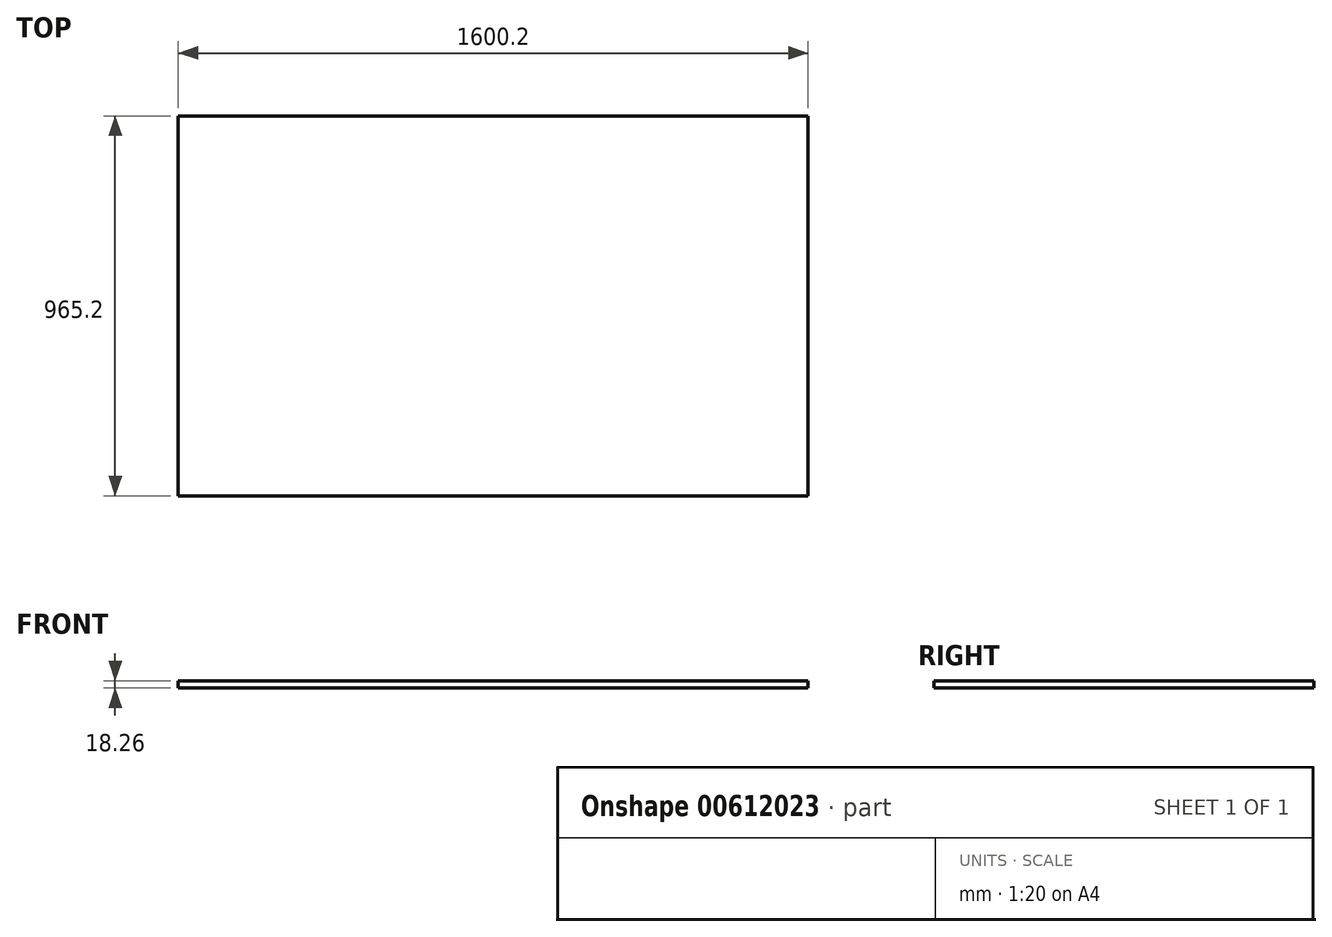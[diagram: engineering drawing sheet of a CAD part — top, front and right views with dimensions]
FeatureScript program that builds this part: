
annotation { "Feature Type Name" : "Feature", "Feature Type Description" : "" }
export const myFeature = defineFeature(function(context is Context, id is Id, definition is map)
    precondition{}
    {
        {
            var Q0;
            Q0=qCreatedBy(makeId("Top.planeOp"),FACE);
            var sketch = newSketch(context, id + "F0", { "sketchPlane" : qUnion([Q0])});
            skLineSegment(sketch, "E0.bottom", {"start": v(-1503.36, 956.1) * mm, "end": v(96.84, 956.1) * mm});
            skLineSegment(sketch, "E0.top", {"start": v(-1503.36, -9.1) * mm, "end": v(96.84, -9.1) * mm});
            skLineSegment(sketch, "E0.left", {"start": v(-1503.36, 956.1) * mm, "end": v(-1503.36, -9.1) * mm});
            skLineSegment(sketch, "E0.right", {"start": v(96.84, 956.1) * mm, "end": v(96.84, -9.1) * mm});
            skLineSegment(sketch, "E1", {"start": v(-1503.36, -9.1) * mm, "end": v(-1363.66, -9.1) * mm, "construction": true});
            skLineSegment(sketch, "E2", {"start": v(-1363.66, -9.1) * mm, "end": v(-1363.66, 956.1) * mm, "construction": true});
            skLineSegment(sketch, "E3", {"start": v(96.84, 956.1) * mm, "end": v(-42.86, 956.1) * mm, "construction": true});
            skLineSegment(sketch, "E4", {"start": v(-42.86, 956.1) * mm, "end": v(-42.86, -9.1) * mm, "construction": true});
            skLineSegment(sketch, "E5", {"start": v(96.84, -9.1) * mm, "end": v(96.84, 130.6) * mm, "construction": true});
            skLineSegment(sketch, "E6", {"start": v(96.84, 130.6) * mm, "end": v(-1503.36, 130.6) * mm, "construction": true});
            skLineSegment(sketch, "E7", {"start": v(-1503.36, 956.1) * mm, "end": v(-1503.36, 816.4) * mm, "construction": true});
            skLineSegment(sketch, "E8", {"start": v(-1503.36, 816.4) * mm, "end": v(96.84, 816.4) * mm, "construction": true});
            skPoint(sketch, "E9", {"position": v(-1363.66, 816.4) * mm});
            skPoint(sketch, "E10", {"position": v(-1363.66, 130.6) * mm});
            skPoint(sketch, "E11", {"position": v(-42.86, 130.6) * mm});
            skPoint(sketch, "E12", {"position": v(-42.86, 816.4) * mm});
            skLineSegment(sketch, "E13", {"start": v(-1363.66, 816.4) * mm, "end": v(-1363.66, 803.7) * mm, "construction": true});
            skLineSegment(sketch, "E14", {"start": v(-1363.66, 803.7) * mm, "end": v(-1350.96, 803.7) * mm, "construction": true});
            skLineSegment(sketch, "E15", {"start": v(-1350.96, 803.7) * mm, "end": v(-1350.96, 816.4) * mm, "construction": true});
            skLineSegment(sketch, "E16", {"start": v(-42.86, 816.4) * mm, "end": v(-55.56, 816.4) * mm, "construction": true});
            skLineSegment(sketch, "E17", {"start": v(-55.56, 816.4) * mm, "end": v(-55.56, 803.7) * mm, "construction": true});
            skLineSegment(sketch, "E18", {"start": v(-1363.66, 130.6) * mm, "end": v(-1350.96, 130.6) * mm});
            skLineSegment(sketch, "E19", {"start": v(-1350.96, 130.6) * mm, "end": v(-1350.96, 143.3) * mm});
            skLineSegment(sketch, "E20", {"start": v(-42.86, 130.6) * mm, "end": v(-55.56, 130.6) * mm});
            skLineSegment(sketch, "E21", {"start": v(-55.56, 130.6) * mm, "end": v(-55.56, 143.3) * mm});
            skLineSegment(sketch, "E22", {"start": v(-1350.96, 143.3) * mm, "end": v(-1122.36, 143.3) * mm});
            skLineSegment(sketch, "E23.0.1.0", {"start": v(-1350.96, 194.1) * mm, "end": v(-1122.36, 194.1) * mm});
            skLineSegment(sketch, "E23.0.2.0", {"start": v(-1350.96, 245.15) * mm, "end": v(-1122.36, 245.15) * mm});
            skLineSegment(sketch, "E23.0.3.0", {"start": v(-1350.96, 295.95) * mm, "end": v(-1122.36, 295.95) * mm});
            skLineSegment(sketch, "E23.0.4.0", {"start": v(-1350.96, 346.75) * mm, "end": v(-1122.36, 346.75) * mm});
            skLineSegment(sketch, "E23.0.5.0", {"start": v(-1350.96, 397.55) * mm, "end": v(-1122.36, 397.55) * mm});
            skLineSegment(sketch, "E23.0.6.0", {"start": v(-1350.96, 448.35) * mm, "end": v(-1122.36, 448.35) * mm});
            skLineSegment(sketch, "E23.0.7.0", {"start": v(-1350.96, 499.15) * mm, "end": v(-1122.36, 499.15) * mm});
            skLineSegment(sketch, "E23.1.0.0", {"start": v(-1300.16, 143.55) * mm, "end": v(-1071.56, 143.55) * mm});
            skLineSegment(sketch, "E23.1.1.0", {"start": v(-1300.16, 194.35) * mm, "end": v(-1071.56, 194.35) * mm});
            skLineSegment(sketch, "E23.1.2.0", {"start": v(-1300.16, 245.15) * mm, "end": v(-1071.56, 245.15) * mm});
            skLineSegment(sketch, "E23.1.3.0", {"start": v(-1300.16, 295.95) * mm, "end": v(-1071.56, 295.95) * mm});
            skLineSegment(sketch, "E23.1.4.0", {"start": v(-1300.16, 346.75) * mm, "end": v(-1071.56, 346.75) * mm});
            skLineSegment(sketch, "E23.1.5.0", {"start": v(-1300.16, 397.55) * mm, "end": v(-1071.56, 397.55) * mm});
            skLineSegment(sketch, "E23.1.6.0", {"start": v(-1300.16, 448.35) * mm, "end": v(-1071.56, 448.35) * mm});
            skLineSegment(sketch, "E23.1.7.0", {"start": v(-1300.16, 499.15) * mm, "end": v(-1071.56, 499.15) * mm});
            skLineSegment(sketch, "E23.2.0.0", {"start": v(-1249.36, 143.55) * mm, "end": v(-1020.76, 143.55) * mm});
            skLineSegment(sketch, "E23.2.1.0", {"start": v(-1249.36, 194.35) * mm, "end": v(-1020.76, 194.35) * mm});
            skLineSegment(sketch, "E23.2.2.0", {"start": v(-1249.36, 245.15) * mm, "end": v(-1020.76, 245.15) * mm});
            skLineSegment(sketch, "E23.2.3.0", {"start": v(-1249.36, 295.95) * mm, "end": v(-1020.76, 295.95) * mm});
            skLineSegment(sketch, "E23.2.4.0", {"start": v(-1249.36, 346.75) * mm, "end": v(-1020.76, 346.75) * mm});
            skLineSegment(sketch, "E23.2.5.0", {"start": v(-1249.36, 397.55) * mm, "end": v(-1020.76, 397.55) * mm});
            skLineSegment(sketch, "E23.2.6.0", {"start": v(-1249.36, 448.35) * mm, "end": v(-1020.76, 448.35) * mm});
            skLineSegment(sketch, "E23.2.7.0", {"start": v(-1249.36, 499.15) * mm, "end": v(-1020.76, 499.15) * mm});
            skLineSegment(sketch, "E23.3.0.0", {"start": v(-1198.56, 143.55) * mm, "end": v(-969.96, 143.55) * mm});
            skLineSegment(sketch, "E23.3.1.0", {"start": v(-1198.56, 194.35) * mm, "end": v(-969.96, 194.35) * mm});
            skLineSegment(sketch, "E23.3.2.0", {"start": v(-1198.56, 245.15) * mm, "end": v(-969.96, 245.15) * mm});
            skLineSegment(sketch, "E23.3.3.0", {"start": v(-1198.56, 295.95) * mm, "end": v(-969.96, 295.95) * mm});
            skLineSegment(sketch, "E23.3.4.0", {"start": v(-1198.56, 346.75) * mm, "end": v(-969.96, 346.75) * mm});
            skLineSegment(sketch, "E23.3.5.0", {"start": v(-1198.56, 397.55) * mm, "end": v(-969.96, 397.55) * mm});
            skLineSegment(sketch, "E23.3.6.0", {"start": v(-1198.56, 448.35) * mm, "end": v(-969.96, 448.35) * mm});
            skLineSegment(sketch, "E23.3.7.0", {"start": v(-1198.56, 499.15) * mm, "end": v(-969.96, 499.15) * mm});
            skLineSegment(sketch, "E23.4.0.0", {"start": v(-1147.76, 143.55) * mm, "end": v(-919.16, 143.55) * mm});
            skLineSegment(sketch, "E23.4.1.0", {"start": v(-1147.76, 194.35) * mm, "end": v(-919.16, 194.35) * mm});
            skLineSegment(sketch, "E23.4.2.0", {"start": v(-1147.76, 245.15) * mm, "end": v(-919.16, 245.15) * mm});
            skLineSegment(sketch, "E23.4.3.0", {"start": v(-1147.76, 295.95) * mm, "end": v(-919.16, 295.95) * mm});
            skLineSegment(sketch, "E23.4.4.0", {"start": v(-1147.76, 346.75) * mm, "end": v(-919.16, 346.75) * mm});
            skLineSegment(sketch, "E23.4.5.0", {"start": v(-1147.76, 397.55) * mm, "end": v(-919.16, 397.55) * mm});
            skLineSegment(sketch, "E23.4.6.0", {"start": v(-1147.76, 448.35) * mm, "end": v(-919.16, 448.35) * mm});
            skLineSegment(sketch, "E23.4.7.0", {"start": v(-1147.76, 499.15) * mm, "end": v(-919.16, 499.15) * mm});
            skLineSegment(sketch, "E23.5.0.0", {"start": v(-1096.96, 143.55) * mm, "end": v(-868.36, 143.55) * mm});
            skLineSegment(sketch, "E23.5.1.0", {"start": v(-1096.96, 194.35) * mm, "end": v(-868.36, 194.35) * mm});
            skLineSegment(sketch, "E23.5.2.0", {"start": v(-1096.96, 245.15) * mm, "end": v(-868.36, 245.15) * mm});
            skLineSegment(sketch, "E23.5.3.0", {"start": v(-1096.96, 295.95) * mm, "end": v(-868.36, 295.95) * mm});
            skLineSegment(sketch, "E23.5.4.0", {"start": v(-1096.96, 346.75) * mm, "end": v(-868.36, 346.75) * mm});
            skLineSegment(sketch, "E23.5.5.0", {"start": v(-1096.96, 397.55) * mm, "end": v(-868.36, 397.55) * mm});
            skLineSegment(sketch, "E23.5.6.0", {"start": v(-1096.96, 448.35) * mm, "end": v(-868.36, 448.35) * mm});
            skLineSegment(sketch, "E23.5.7.0", {"start": v(-1096.96, 499.15) * mm, "end": v(-868.36, 499.15) * mm});
            skLineSegment(sketch, "E23.6.0.0", {"start": v(-1046.16, 143.55) * mm, "end": v(-817.56, 143.55) * mm});
            skLineSegment(sketch, "E23.6.1.0", {"start": v(-1046.16, 194.35) * mm, "end": v(-817.56, 194.35) * mm});
            skLineSegment(sketch, "E23.6.2.0", {"start": v(-1046.16, 245.15) * mm, "end": v(-817.56, 245.15) * mm});
            skLineSegment(sketch, "E23.6.3.0", {"start": v(-1046.16, 295.95) * mm, "end": v(-817.56, 295.95) * mm});
            skLineSegment(sketch, "E23.6.4.0", {"start": v(-1046.16, 346.75) * mm, "end": v(-817.56, 346.75) * mm});
            skLineSegment(sketch, "E23.6.5.0", {"start": v(-1046.16, 397.55) * mm, "end": v(-817.56, 397.55) * mm});
            skLineSegment(sketch, "E23.6.6.0", {"start": v(-1046.16, 448.35) * mm, "end": v(-817.56, 448.35) * mm});
            skLineSegment(sketch, "E23.6.7.0", {"start": v(-1046.16, 499.15) * mm, "end": v(-817.56, 499.15) * mm});
            skLineSegment(sketch, "E23.7.0.0", {"start": v(-995.36, 143.55) * mm, "end": v(-766.76, 143.55) * mm});
            skLineSegment(sketch, "E23.7.1.0", {"start": v(-995.36, 194.35) * mm, "end": v(-766.76, 194.35) * mm});
            skLineSegment(sketch, "E23.7.2.0", {"start": v(-995.36, 245.15) * mm, "end": v(-766.76, 245.15) * mm});
            skLineSegment(sketch, "E23.7.3.0", {"start": v(-995.36, 295.95) * mm, "end": v(-766.76, 295.95) * mm});
            skLineSegment(sketch, "E23.7.4.0", {"start": v(-995.36, 346.75) * mm, "end": v(-766.76, 346.75) * mm});
            skLineSegment(sketch, "E23.7.5.0", {"start": v(-995.36, 397.55) * mm, "end": v(-766.76, 397.55) * mm});
            skLineSegment(sketch, "E23.7.6.0", {"start": v(-995.36, 448.35) * mm, "end": v(-766.76, 448.35) * mm});
            skLineSegment(sketch, "E23.7.7.0", {"start": v(-995.36, 499.15) * mm, "end": v(-766.76, 499.15) * mm});
            skLineSegment(sketch, "E23.8.0.0", {"start": v(-944.56, 143.55) * mm, "end": v(-715.96, 143.55) * mm});
            skLineSegment(sketch, "E23.8.1.0", {"start": v(-944.56, 194.35) * mm, "end": v(-715.96, 194.35) * mm});
            skLineSegment(sketch, "E23.8.2.0", {"start": v(-944.56, 245.15) * mm, "end": v(-715.96, 245.15) * mm});
            skLineSegment(sketch, "E23.8.3.0", {"start": v(-944.56, 295.95) * mm, "end": v(-715.96, 295.95) * mm});
            skLineSegment(sketch, "E23.8.4.0", {"start": v(-944.56, 346.75) * mm, "end": v(-715.96, 346.75) * mm});
            skLineSegment(sketch, "E23.8.5.0", {"start": v(-944.56, 397.55) * mm, "end": v(-715.96, 397.55) * mm});
            skLineSegment(sketch, "E23.8.6.0", {"start": v(-944.56, 448.35) * mm, "end": v(-715.96, 448.35) * mm});
            skLineSegment(sketch, "E23.8.7.0", {"start": v(-944.56, 499.15) * mm, "end": v(-715.96, 499.15) * mm});
            skLineSegment(sketch, "E23.9.0.0", {"start": v(-893.76, 143.55) * mm, "end": v(-665.16, 143.55) * mm});
            skLineSegment(sketch, "E23.9.1.0", {"start": v(-893.76, 194.35) * mm, "end": v(-665.16, 194.35) * mm});
            skLineSegment(sketch, "E23.9.2.0", {"start": v(-893.76, 245.15) * mm, "end": v(-665.16, 245.15) * mm});
            skLineSegment(sketch, "E23.9.3.0", {"start": v(-893.76, 295.95) * mm, "end": v(-665.16, 295.95) * mm});
            skLineSegment(sketch, "E23.9.4.0", {"start": v(-893.76, 346.75) * mm, "end": v(-665.16, 346.75) * mm});
            skLineSegment(sketch, "E23.9.5.0", {"start": v(-893.76, 397.55) * mm, "end": v(-665.16, 397.55) * mm});
            skLineSegment(sketch, "E23.9.6.0", {"start": v(-893.76, 448.35) * mm, "end": v(-665.16, 448.35) * mm});
            skLineSegment(sketch, "E23.9.7.0", {"start": v(-893.76, 499.15) * mm, "end": v(-665.16, 499.15) * mm});
            skLineSegment(sketch, "E23.10.0.0", {"start": v(-842.96, 143.55) * mm, "end": v(-614.36, 143.55) * mm});
            skLineSegment(sketch, "E23.10.1.0", {"start": v(-842.96, 194.35) * mm, "end": v(-614.36, 194.35) * mm});
            skLineSegment(sketch, "E23.10.2.0", {"start": v(-842.96, 245.15) * mm, "end": v(-614.36, 245.15) * mm});
            skLineSegment(sketch, "E23.10.3.0", {"start": v(-842.96, 295.95) * mm, "end": v(-614.36, 295.95) * mm});
            skLineSegment(sketch, "E23.10.4.0", {"start": v(-842.96, 346.75) * mm, "end": v(-614.36, 346.75) * mm});
            skLineSegment(sketch, "E23.10.5.0", {"start": v(-842.96, 397.55) * mm, "end": v(-614.36, 397.55) * mm});
            skLineSegment(sketch, "E23.10.6.0", {"start": v(-842.96, 448.35) * mm, "end": v(-614.36, 448.35) * mm});
            skLineSegment(sketch, "E23.10.7.0", {"start": v(-842.96, 499.15) * mm, "end": v(-614.36, 499.15) * mm});
            skLineSegment(sketch, "E23.11.0.0", {"start": v(-792.16, 143.55) * mm, "end": v(-563.56, 143.55) * mm});
            skLineSegment(sketch, "E23.11.1.0", {"start": v(-792.16, 194.35) * mm, "end": v(-563.56, 194.35) * mm});
            skLineSegment(sketch, "E23.11.2.0", {"start": v(-792.16, 245.15) * mm, "end": v(-563.56, 245.15) * mm});
            skLineSegment(sketch, "E23.11.3.0", {"start": v(-792.16, 295.95) * mm, "end": v(-563.56, 295.95) * mm});
            skLineSegment(sketch, "E23.11.4.0", {"start": v(-792.16, 346.75) * mm, "end": v(-563.56, 346.75) * mm});
            skLineSegment(sketch, "E23.11.5.0", {"start": v(-792.16, 397.55) * mm, "end": v(-563.56, 397.55) * mm});
            skLineSegment(sketch, "E23.11.6.0", {"start": v(-792.16, 448.35) * mm, "end": v(-563.56, 448.35) * mm});
            skLineSegment(sketch, "E23.11.7.0", {"start": v(-792.16, 499.15) * mm, "end": v(-563.56, 499.15) * mm});
            skLineSegment(sketch, "E23.12.0.0", {"start": v(-741.36, 143.55) * mm, "end": v(-512.76, 143.55) * mm});
            skLineSegment(sketch, "E23.12.1.0", {"start": v(-741.36, 194.35) * mm, "end": v(-512.76, 194.35) * mm});
            skLineSegment(sketch, "E23.12.2.0", {"start": v(-741.36, 245.15) * mm, "end": v(-512.76, 245.15) * mm});
            skLineSegment(sketch, "E23.12.3.0", {"start": v(-741.36, 295.95) * mm, "end": v(-512.76, 295.95) * mm});
            skLineSegment(sketch, "E23.12.4.0", {"start": v(-741.36, 346.75) * mm, "end": v(-512.76, 346.75) * mm});
            skLineSegment(sketch, "E23.12.5.0", {"start": v(-741.36, 397.55) * mm, "end": v(-512.76, 397.55) * mm});
            skLineSegment(sketch, "E23.12.6.0", {"start": v(-741.36, 448.35) * mm, "end": v(-512.76, 448.35) * mm});
            skLineSegment(sketch, "E23.12.7.0", {"start": v(-741.36, 499.15) * mm, "end": v(-512.76, 499.15) * mm});
            skLineSegment(sketch, "E23.13.0.0", {"start": v(-690.56, 143.55) * mm, "end": v(-461.96, 143.55) * mm});
            skLineSegment(sketch, "E23.13.1.0", {"start": v(-690.56, 194.35) * mm, "end": v(-461.96, 194.35) * mm});
            skLineSegment(sketch, "E23.13.2.0", {"start": v(-690.56, 245.15) * mm, "end": v(-461.96, 245.15) * mm});
            skLineSegment(sketch, "E23.13.3.0", {"start": v(-690.56, 295.95) * mm, "end": v(-461.96, 295.95) * mm});
            skLineSegment(sketch, "E23.13.4.0", {"start": v(-690.56, 346.75) * mm, "end": v(-461.96, 346.75) * mm});
            skLineSegment(sketch, "E23.13.5.0", {"start": v(-690.56, 397.55) * mm, "end": v(-461.96, 397.55) * mm});
            skLineSegment(sketch, "E23.13.6.0", {"start": v(-690.56, 448.35) * mm, "end": v(-461.96, 448.35) * mm});
            skLineSegment(sketch, "E23.13.7.0", {"start": v(-690.56, 499.15) * mm, "end": v(-461.96, 499.15) * mm});
            skLineSegment(sketch, "E23.14.0.0", {"start": v(-639.76, 143.55) * mm, "end": v(-411.16, 143.55) * mm});
            skLineSegment(sketch, "E23.14.1.0", {"start": v(-639.76, 194.35) * mm, "end": v(-411.16, 194.35) * mm});
            skLineSegment(sketch, "E23.14.2.0", {"start": v(-639.76, 245.15) * mm, "end": v(-411.16, 245.15) * mm});
            skLineSegment(sketch, "E23.14.3.0", {"start": v(-639.76, 295.95) * mm, "end": v(-411.16, 295.95) * mm});
            skLineSegment(sketch, "E23.14.4.0", {"start": v(-639.76, 346.75) * mm, "end": v(-411.16, 346.75) * mm});
            skLineSegment(sketch, "E23.14.5.0", {"start": v(-639.76, 397.55) * mm, "end": v(-411.16, 397.55) * mm});
            skLineSegment(sketch, "E23.14.6.0", {"start": v(-639.76, 448.35) * mm, "end": v(-411.16, 448.35) * mm});
            skLineSegment(sketch, "E23.14.7.0", {"start": v(-639.76, 499.15) * mm, "end": v(-411.16, 499.15) * mm});
            skLineSegment(sketch, "E23.15.0.0", {"start": v(-588.96, 143.55) * mm, "end": v(-360.36, 143.55) * mm});
            skLineSegment(sketch, "E23.15.1.0", {"start": v(-588.96, 194.35) * mm, "end": v(-360.36, 194.35) * mm});
            skLineSegment(sketch, "E23.15.2.0", {"start": v(-588.96, 245.15) * mm, "end": v(-360.36, 245.15) * mm});
            skLineSegment(sketch, "E23.15.3.0", {"start": v(-588.96, 295.95) * mm, "end": v(-360.36, 295.95) * mm});
            skLineSegment(sketch, "E23.15.4.0", {"start": v(-588.96, 346.75) * mm, "end": v(-360.36, 346.75) * mm});
            skLineSegment(sketch, "E23.15.5.0", {"start": v(-588.96, 397.55) * mm, "end": v(-360.36, 397.55) * mm});
            skLineSegment(sketch, "E23.15.6.0", {"start": v(-588.96, 448.35) * mm, "end": v(-360.36, 448.35) * mm});
            skLineSegment(sketch, "E23.15.7.0", {"start": v(-588.96, 499.15) * mm, "end": v(-360.36, 499.15) * mm});
            skLineSegment(sketch, "E23.16.0.0", {"start": v(-538.16, 143.55) * mm, "end": v(-309.56, 143.55) * mm});
            skLineSegment(sketch, "E23.16.1.0", {"start": v(-538.16, 194.35) * mm, "end": v(-309.56, 194.35) * mm});
            skLineSegment(sketch, "E23.16.2.0", {"start": v(-538.16, 245.15) * mm, "end": v(-309.56, 245.15) * mm});
            skLineSegment(sketch, "E23.16.3.0", {"start": v(-538.16, 295.95) * mm, "end": v(-309.56, 295.95) * mm});
            skLineSegment(sketch, "E23.16.4.0", {"start": v(-538.16, 346.75) * mm, "end": v(-309.56, 346.75) * mm});
            skLineSegment(sketch, "E23.16.5.0", {"start": v(-538.16, 397.55) * mm, "end": v(-309.56, 397.55) * mm});
            skLineSegment(sketch, "E23.16.6.0", {"start": v(-538.16, 448.35) * mm, "end": v(-309.56, 448.35) * mm});
            skLineSegment(sketch, "E23.16.7.0", {"start": v(-538.16, 499.15) * mm, "end": v(-309.56, 499.15) * mm});
            skLineSegment(sketch, "E23.direction2", {"start": v(-1350.96, 143.3) * mm, "end": v(-1350.96, 194.1) * mm, "construction": true});
            skLineSegment(sketch, "E24.0.17.0", {"start": v(-487.36, 143.55) * mm, "end": v(-258.76, 143.55) * mm});
            skLineSegment(sketch, "E24.0.17.1", {"start": v(-487.36, 194.35) * mm, "end": v(-258.76, 194.35) * mm});
            skLineSegment(sketch, "E24.0.17.2", {"start": v(-487.36, 245.15) * mm, "end": v(-258.76, 245.15) * mm});
            skLineSegment(sketch, "E24.0.17.3", {"start": v(-487.36, 295.95) * mm, "end": v(-258.76, 295.95) * mm});
            skLineSegment(sketch, "E24.0.17.4", {"start": v(-487.36, 346.75) * mm, "end": v(-258.76, 346.75) * mm});
            skLineSegment(sketch, "E24.0.17.5", {"start": v(-487.36, 397.55) * mm, "end": v(-258.76, 397.55) * mm});
            skLineSegment(sketch, "E24.0.17.6", {"start": v(-487.36, 448.35) * mm, "end": v(-258.76, 448.35) * mm});
            skLineSegment(sketch, "E24.0.17.7", {"start": v(-487.36, 499.15) * mm, "end": v(-258.76, 499.15) * mm});
            skLineSegment(sketch, "E24.0.18.0", {"start": v(-436.56, 143.55) * mm, "end": v(-207.96, 143.55) * mm});
            skLineSegment(sketch, "E24.0.18.1", {"start": v(-436.56, 194.35) * mm, "end": v(-207.96, 194.35) * mm});
            skLineSegment(sketch, "E24.0.18.2", {"start": v(-436.56, 245.15) * mm, "end": v(-207.96, 245.15) * mm});
            skLineSegment(sketch, "E24.0.18.3", {"start": v(-436.56, 295.95) * mm, "end": v(-207.96, 295.95) * mm});
            skLineSegment(sketch, "E24.0.18.4", {"start": v(-436.56, 346.75) * mm, "end": v(-207.96, 346.75) * mm});
            skLineSegment(sketch, "E24.0.18.5", {"start": v(-436.56, 397.55) * mm, "end": v(-207.96, 397.55) * mm});
            skLineSegment(sketch, "E24.0.18.6", {"start": v(-436.56, 448.35) * mm, "end": v(-207.96, 448.35) * mm});
            skLineSegment(sketch, "E24.0.18.7", {"start": v(-436.56, 499.15) * mm, "end": v(-207.96, 499.15) * mm});
            skLineSegment(sketch, "E24.0.19.0", {"start": v(-385.76, 143.55) * mm, "end": v(-157.16, 143.55) * mm});
            skLineSegment(sketch, "E24.0.19.1", {"start": v(-385.76, 194.35) * mm, "end": v(-157.16, 194.35) * mm});
            skLineSegment(sketch, "E24.0.19.2", {"start": v(-385.76, 245.15) * mm, "end": v(-157.16, 245.15) * mm});
            skLineSegment(sketch, "E24.0.19.3", {"start": v(-385.76, 295.95) * mm, "end": v(-157.16, 295.95) * mm});
            skLineSegment(sketch, "E24.0.19.4", {"start": v(-385.76, 346.75) * mm, "end": v(-157.16, 346.75) * mm});
            skLineSegment(sketch, "E24.0.19.5", {"start": v(-385.76, 397.55) * mm, "end": v(-157.16, 397.55) * mm});
            skLineSegment(sketch, "E24.0.19.6", {"start": v(-385.76, 448.35) * mm, "end": v(-157.16, 448.35) * mm});
            skLineSegment(sketch, "E24.0.19.7", {"start": v(-385.76, 499.15) * mm, "end": v(-157.16, 499.15) * mm});
            skLineSegment(sketch, "E25.0.0.8", {"start": v(-1350.96, 549.95) * mm, "end": v(-1122.36, 549.95) * mm});
            skLineSegment(sketch, "E25.0.0.9", {"start": v(-1350.96, 600.75) * mm, "end": v(-1122.36, 600.75) * mm});
            skLineSegment(sketch, "E25.0.0.10", {"start": v(-1350.96, 651.55) * mm, "end": v(-1122.36, 651.55) * mm});
            skLineSegment(sketch, "E25.0.0.11", {"start": v(-1350.96, 702.35) * mm, "end": v(-1122.36, 702.35) * mm});
            skLineSegment(sketch, "E25.0.0.12", {"start": v(-1350.96, 753.15) * mm, "end": v(-1122.36, 753.15) * mm});
            skLineSegment(sketch, "E25.0.0.13", {"start": v(-1350.96, 803.95) * mm, "end": v(-1122.36, 803.95) * mm});
            skLineSegment(sketch, "E25.0.1.8", {"start": v(-1300.16, 549.95) * mm, "end": v(-1071.56, 549.95) * mm});
            skLineSegment(sketch, "E25.0.1.9", {"start": v(-1300.16, 600.75) * mm, "end": v(-1071.56, 600.75) * mm});
            skLineSegment(sketch, "E25.0.1.10", {"start": v(-1300.16, 651.55) * mm, "end": v(-1071.56, 651.55) * mm});
            skLineSegment(sketch, "E25.0.1.11", {"start": v(-1300.16, 702.35) * mm, "end": v(-1071.56, 702.35) * mm});
            skLineSegment(sketch, "E25.0.1.12", {"start": v(-1300.16, 753.15) * mm, "end": v(-1071.56, 753.15) * mm});
            skLineSegment(sketch, "E25.0.1.13", {"start": v(-1300.16, 803.95) * mm, "end": v(-1071.56, 803.95) * mm});
            skLineSegment(sketch, "E25.0.2.8", {"start": v(-1249.36, 549.95) * mm, "end": v(-1020.76, 549.95) * mm});
            skLineSegment(sketch, "E25.0.2.9", {"start": v(-1249.36, 600.75) * mm, "end": v(-1020.76, 600.75) * mm});
            skLineSegment(sketch, "E25.0.2.10", {"start": v(-1249.36, 651.55) * mm, "end": v(-1020.76, 651.55) * mm});
            skLineSegment(sketch, "E25.0.2.11", {"start": v(-1249.36, 702.35) * mm, "end": v(-1020.76, 702.35) * mm});
            skLineSegment(sketch, "E25.0.2.12", {"start": v(-1249.36, 753.15) * mm, "end": v(-1020.76, 753.15) * mm});
            skLineSegment(sketch, "E25.0.2.13", {"start": v(-1249.36, 803.95) * mm, "end": v(-1020.76, 803.95) * mm});
            skLineSegment(sketch, "E25.0.3.8", {"start": v(-1198.56, 549.95) * mm, "end": v(-969.96, 549.95) * mm});
            skLineSegment(sketch, "E25.0.3.9", {"start": v(-1198.56, 600.75) * mm, "end": v(-969.96, 600.75) * mm});
            skLineSegment(sketch, "E25.0.3.10", {"start": v(-1198.56, 651.55) * mm, "end": v(-969.96, 651.55) * mm});
            skLineSegment(sketch, "E25.0.3.11", {"start": v(-1198.56, 702.35) * mm, "end": v(-969.96, 702.35) * mm});
            skLineSegment(sketch, "E25.0.3.12", {"start": v(-1198.56, 753.15) * mm, "end": v(-969.96, 753.15) * mm});
            skLineSegment(sketch, "E25.0.3.13", {"start": v(-1198.56, 803.95) * mm, "end": v(-969.96, 803.95) * mm});
            skLineSegment(sketch, "E25.0.4.8", {"start": v(-1147.76, 549.95) * mm, "end": v(-919.16, 549.95) * mm});
            skLineSegment(sketch, "E25.0.4.9", {"start": v(-1147.76, 600.75) * mm, "end": v(-919.16, 600.75) * mm});
            skLineSegment(sketch, "E25.0.4.10", {"start": v(-1147.76, 651.55) * mm, "end": v(-919.16, 651.55) * mm});
            skLineSegment(sketch, "E25.0.4.11", {"start": v(-1147.76, 702.35) * mm, "end": v(-919.16, 702.35) * mm});
            skLineSegment(sketch, "E25.0.4.12", {"start": v(-1147.76, 753.15) * mm, "end": v(-919.16, 753.15) * mm});
            skLineSegment(sketch, "E25.0.4.13", {"start": v(-1147.76, 803.95) * mm, "end": v(-919.16, 803.95) * mm});
            skLineSegment(sketch, "E25.0.5.8", {"start": v(-1096.96, 549.95) * mm, "end": v(-868.36, 549.95) * mm});
            skLineSegment(sketch, "E25.0.5.9", {"start": v(-1096.96, 600.75) * mm, "end": v(-868.36, 600.75) * mm});
            skLineSegment(sketch, "E25.0.5.10", {"start": v(-1096.96, 651.55) * mm, "end": v(-868.36, 651.55) * mm});
            skLineSegment(sketch, "E25.0.5.11", {"start": v(-1096.96, 702.35) * mm, "end": v(-868.36, 702.35) * mm});
            skLineSegment(sketch, "E25.0.5.12", {"start": v(-1096.96, 753.15) * mm, "end": v(-868.36, 753.15) * mm});
            skLineSegment(sketch, "E25.0.5.13", {"start": v(-1096.96, 803.95) * mm, "end": v(-868.36, 803.95) * mm});
            skLineSegment(sketch, "E25.0.6.8", {"start": v(-1046.16, 549.95) * mm, "end": v(-817.56, 549.95) * mm});
            skLineSegment(sketch, "E25.0.6.9", {"start": v(-1046.16, 600.75) * mm, "end": v(-817.56, 600.75) * mm});
            skLineSegment(sketch, "E25.0.6.10", {"start": v(-1046.16, 651.55) * mm, "end": v(-817.56, 651.55) * mm});
            skLineSegment(sketch, "E25.0.6.11", {"start": v(-1046.16, 702.35) * mm, "end": v(-817.56, 702.35) * mm});
            skLineSegment(sketch, "E25.0.6.12", {"start": v(-1046.16, 753.15) * mm, "end": v(-817.56, 753.15) * mm});
            skLineSegment(sketch, "E25.0.6.13", {"start": v(-1046.16, 803.95) * mm, "end": v(-817.56, 803.95) * mm});
            skLineSegment(sketch, "E25.0.7.8", {"start": v(-995.36, 549.95) * mm, "end": v(-766.76, 549.95) * mm});
            skLineSegment(sketch, "E25.0.7.9", {"start": v(-995.36, 600.75) * mm, "end": v(-766.76, 600.75) * mm});
            skLineSegment(sketch, "E25.0.7.10", {"start": v(-995.36, 651.55) * mm, "end": v(-766.76, 651.55) * mm});
            skLineSegment(sketch, "E25.0.7.11", {"start": v(-995.36, 702.35) * mm, "end": v(-766.76, 702.35) * mm});
            skLineSegment(sketch, "E25.0.7.12", {"start": v(-995.36, 753.15) * mm, "end": v(-766.76, 753.15) * mm});
            skLineSegment(sketch, "E25.0.7.13", {"start": v(-995.36, 803.95) * mm, "end": v(-766.76, 803.95) * mm});
            skLineSegment(sketch, "E25.0.8.8", {"start": v(-944.56, 549.95) * mm, "end": v(-715.96, 549.95) * mm});
            skLineSegment(sketch, "E25.0.8.9", {"start": v(-944.56, 600.75) * mm, "end": v(-715.96, 600.75) * mm});
            skLineSegment(sketch, "E25.0.8.10", {"start": v(-944.56, 651.55) * mm, "end": v(-715.96, 651.55) * mm});
            skLineSegment(sketch, "E25.0.8.11", {"start": v(-944.56, 702.35) * mm, "end": v(-715.96, 702.35) * mm});
            skLineSegment(sketch, "E25.0.8.12", {"start": v(-944.56, 753.15) * mm, "end": v(-715.96, 753.15) * mm});
            skLineSegment(sketch, "E25.0.8.13", {"start": v(-944.56, 803.95) * mm, "end": v(-715.96, 803.95) * mm});
            skLineSegment(sketch, "E25.0.9.8", {"start": v(-893.76, 549.95) * mm, "end": v(-665.16, 549.95) * mm});
            skLineSegment(sketch, "E25.0.9.9", {"start": v(-893.76, 600.75) * mm, "end": v(-665.16, 600.75) * mm});
            skLineSegment(sketch, "E25.0.9.10", {"start": v(-893.76, 651.55) * mm, "end": v(-665.16, 651.55) * mm});
            skLineSegment(sketch, "E25.0.9.11", {"start": v(-893.76, 702.35) * mm, "end": v(-665.16, 702.35) * mm});
            skLineSegment(sketch, "E25.0.9.12", {"start": v(-893.76, 753.15) * mm, "end": v(-665.16, 753.15) * mm});
            skLineSegment(sketch, "E25.0.9.13", {"start": v(-893.76, 803.95) * mm, "end": v(-665.16, 803.95) * mm});
            skLineSegment(sketch, "E25.0.10.8", {"start": v(-842.96, 549.95) * mm, "end": v(-614.36, 549.95) * mm});
            skLineSegment(sketch, "E25.0.10.9", {"start": v(-842.96, 600.75) * mm, "end": v(-614.36, 600.75) * mm});
            skLineSegment(sketch, "E25.0.10.10", {"start": v(-842.96, 651.55) * mm, "end": v(-614.36, 651.55) * mm});
            skLineSegment(sketch, "E25.0.10.11", {"start": v(-842.96, 702.35) * mm, "end": v(-614.36, 702.35) * mm});
            skLineSegment(sketch, "E25.0.10.12", {"start": v(-842.96, 753.15) * mm, "end": v(-614.36, 753.15) * mm});
            skLineSegment(sketch, "E25.0.10.13", {"start": v(-842.96, 803.95) * mm, "end": v(-614.36, 803.95) * mm});
            skLineSegment(sketch, "E25.0.11.8", {"start": v(-792.16, 549.95) * mm, "end": v(-563.56, 549.95) * mm});
            skLineSegment(sketch, "E25.0.11.9", {"start": v(-792.16, 600.75) * mm, "end": v(-563.56, 600.75) * mm});
            skLineSegment(sketch, "E25.0.11.10", {"start": v(-792.16, 651.55) * mm, "end": v(-563.56, 651.55) * mm});
            skLineSegment(sketch, "E25.0.11.11", {"start": v(-792.16, 702.35) * mm, "end": v(-563.56, 702.35) * mm});
            skLineSegment(sketch, "E25.0.11.12", {"start": v(-792.16, 753.15) * mm, "end": v(-563.56, 753.15) * mm});
            skLineSegment(sketch, "E25.0.11.13", {"start": v(-792.16, 803.95) * mm, "end": v(-563.56, 803.95) * mm});
            skLineSegment(sketch, "E25.0.12.8", {"start": v(-741.36, 549.95) * mm, "end": v(-512.76, 549.95) * mm});
            skLineSegment(sketch, "E25.0.12.9", {"start": v(-741.36, 600.75) * mm, "end": v(-512.76, 600.75) * mm});
            skLineSegment(sketch, "E25.0.12.10", {"start": v(-741.36, 651.55) * mm, "end": v(-512.76, 651.55) * mm});
            skLineSegment(sketch, "E25.0.12.11", {"start": v(-741.36, 702.35) * mm, "end": v(-512.76, 702.35) * mm});
            skLineSegment(sketch, "E25.0.12.12", {"start": v(-741.36, 753.15) * mm, "end": v(-512.76, 753.15) * mm});
            skLineSegment(sketch, "E25.0.12.13", {"start": v(-741.36, 803.95) * mm, "end": v(-512.76, 803.95) * mm});
            skLineSegment(sketch, "E25.0.13.8", {"start": v(-690.56, 549.95) * mm, "end": v(-461.96, 549.95) * mm});
            skLineSegment(sketch, "E25.0.13.9", {"start": v(-690.56, 600.75) * mm, "end": v(-461.96, 600.75) * mm});
            skLineSegment(sketch, "E25.0.13.10", {"start": v(-690.56, 651.55) * mm, "end": v(-461.96, 651.55) * mm});
            skLineSegment(sketch, "E25.0.13.11", {"start": v(-690.56, 702.35) * mm, "end": v(-461.96, 702.35) * mm});
            skLineSegment(sketch, "E25.0.13.12", {"start": v(-690.56, 753.15) * mm, "end": v(-461.96, 753.15) * mm});
            skLineSegment(sketch, "E25.0.13.13", {"start": v(-690.56, 803.95) * mm, "end": v(-461.96, 803.95) * mm});
            skLineSegment(sketch, "E25.0.14.8", {"start": v(-639.76, 549.95) * mm, "end": v(-411.16, 549.95) * mm});
            skLineSegment(sketch, "E25.0.14.9", {"start": v(-639.76, 600.75) * mm, "end": v(-411.16, 600.75) * mm});
            skLineSegment(sketch, "E25.0.14.10", {"start": v(-639.76, 651.55) * mm, "end": v(-411.16, 651.55) * mm});
            skLineSegment(sketch, "E25.0.14.11", {"start": v(-639.76, 702.35) * mm, "end": v(-411.16, 702.35) * mm});
            skLineSegment(sketch, "E25.0.14.12", {"start": v(-639.76, 753.15) * mm, "end": v(-411.16, 753.15) * mm});
            skLineSegment(sketch, "E25.0.14.13", {"start": v(-639.76, 803.95) * mm, "end": v(-411.16, 803.95) * mm});
            skLineSegment(sketch, "E25.0.15.8", {"start": v(-588.96, 549.95) * mm, "end": v(-360.36, 549.95) * mm});
            skLineSegment(sketch, "E25.0.15.9", {"start": v(-588.96, 600.75) * mm, "end": v(-360.36, 600.75) * mm});
            skLineSegment(sketch, "E25.0.15.10", {"start": v(-588.96, 651.55) * mm, "end": v(-360.36, 651.55) * mm});
            skLineSegment(sketch, "E25.0.15.11", {"start": v(-588.96, 702.35) * mm, "end": v(-360.36, 702.35) * mm});
            skLineSegment(sketch, "E25.0.15.12", {"start": v(-588.96, 753.15) * mm, "end": v(-360.36, 753.15) * mm});
            skLineSegment(sketch, "E25.0.15.13", {"start": v(-588.96, 803.95) * mm, "end": v(-360.36, 803.95) * mm});
            skLineSegment(sketch, "E25.0.16.8", {"start": v(-538.16, 549.95) * mm, "end": v(-309.56, 549.95) * mm});
            skLineSegment(sketch, "E25.0.16.9", {"start": v(-538.16, 600.75) * mm, "end": v(-309.56, 600.75) * mm});
            skLineSegment(sketch, "E25.0.16.10", {"start": v(-538.16, 651.55) * mm, "end": v(-309.56, 651.55) * mm});
            skLineSegment(sketch, "E25.0.16.11", {"start": v(-538.16, 702.35) * mm, "end": v(-309.56, 702.35) * mm});
            skLineSegment(sketch, "E25.0.16.12", {"start": v(-538.16, 753.15) * mm, "end": v(-309.56, 753.15) * mm});
            skLineSegment(sketch, "E25.0.16.13", {"start": v(-538.16, 803.95) * mm, "end": v(-309.56, 803.95) * mm});
            skLineSegment(sketch, "E25.0.17.8", {"start": v(-487.36, 549.95) * mm, "end": v(-258.76, 549.95) * mm});
            skLineSegment(sketch, "E25.0.17.9", {"start": v(-487.36, 600.75) * mm, "end": v(-258.76, 600.75) * mm});
            skLineSegment(sketch, "E25.0.17.10", {"start": v(-487.36, 651.55) * mm, "end": v(-258.76, 651.55) * mm});
            skLineSegment(sketch, "E25.0.17.11", {"start": v(-487.36, 702.35) * mm, "end": v(-258.76, 702.35) * mm});
            skLineSegment(sketch, "E25.0.17.12", {"start": v(-487.36, 753.15) * mm, "end": v(-258.76, 753.15) * mm});
            skLineSegment(sketch, "E25.0.17.13", {"start": v(-487.36, 803.95) * mm, "end": v(-258.76, 803.95) * mm});
            skLineSegment(sketch, "E25.0.18.8", {"start": v(-436.56, 549.95) * mm, "end": v(-207.96, 549.95) * mm});
            skLineSegment(sketch, "E25.0.18.9", {"start": v(-436.56, 600.75) * mm, "end": v(-207.96, 600.75) * mm});
            skLineSegment(sketch, "E25.0.18.10", {"start": v(-436.56, 651.55) * mm, "end": v(-207.96, 651.55) * mm});
            skLineSegment(sketch, "E25.0.18.11", {"start": v(-436.56, 702.35) * mm, "end": v(-207.96, 702.35) * mm});
            skLineSegment(sketch, "E25.0.18.12", {"start": v(-436.56, 753.15) * mm, "end": v(-207.96, 753.15) * mm});
            skLineSegment(sketch, "E25.0.18.13", {"start": v(-436.56, 803.95) * mm, "end": v(-207.96, 803.95) * mm});
            skLineSegment(sketch, "E25.0.19.8", {"start": v(-385.76, 549.95) * mm, "end": v(-157.16, 549.95) * mm});
            skLineSegment(sketch, "E25.0.19.9", {"start": v(-385.76, 600.75) * mm, "end": v(-157.16, 600.75) * mm});
            skLineSegment(sketch, "E25.0.19.10", {"start": v(-385.76, 651.55) * mm, "end": v(-157.16, 651.55) * mm});
            skLineSegment(sketch, "E25.0.19.11", {"start": v(-385.76, 702.35) * mm, "end": v(-157.16, 702.35) * mm});
            skLineSegment(sketch, "E25.0.19.12", {"start": v(-385.76, 753.15) * mm, "end": v(-157.16, 753.15) * mm});
            skLineSegment(sketch, "E25.0.19.13", {"start": v(-385.76, 803.95) * mm, "end": v(-157.16, 803.95) * mm});
            skLineSegment(sketch, "E26.0.20.0", {"start": v(-334.96, 143.55) * mm, "end": v(-106.36, 143.55) * mm});
            skLineSegment(sketch, "E26.0.20.1", {"start": v(-334.96, 194.35) * mm, "end": v(-106.36, 194.35) * mm});
            skLineSegment(sketch, "E26.0.20.2", {"start": v(-334.96, 245.15) * mm, "end": v(-106.36, 245.15) * mm});
            skLineSegment(sketch, "E26.0.20.3", {"start": v(-334.96, 295.95) * mm, "end": v(-106.36, 295.95) * mm});
            skLineSegment(sketch, "E26.0.20.4", {"start": v(-334.96, 346.75) * mm, "end": v(-106.36, 346.75) * mm});
            skLineSegment(sketch, "E26.0.20.5", {"start": v(-334.96, 397.55) * mm, "end": v(-106.36, 397.55) * mm});
            skLineSegment(sketch, "E26.0.20.6", {"start": v(-334.96, 448.35) * mm, "end": v(-106.36, 448.35) * mm});
            skLineSegment(sketch, "E26.0.20.7", {"start": v(-334.96, 499.15) * mm, "end": v(-106.36, 499.15) * mm});
            skLineSegment(sketch, "E26.0.20.8", {"start": v(-334.96, 549.95) * mm, "end": v(-106.36, 549.95) * mm});
            skLineSegment(sketch, "E26.0.20.9", {"start": v(-334.96, 600.75) * mm, "end": v(-106.36, 600.75) * mm});
            skLineSegment(sketch, "E26.0.20.10", {"start": v(-334.96, 651.55) * mm, "end": v(-106.36, 651.55) * mm});
            skLineSegment(sketch, "E26.0.20.11", {"start": v(-334.96, 702.35) * mm, "end": v(-106.36, 702.35) * mm});
            skLineSegment(sketch, "E26.0.20.12", {"start": v(-334.96, 753.15) * mm, "end": v(-106.36, 753.15) * mm});
            skLineSegment(sketch, "E26.0.20.13", {"start": v(-334.96, 803.95) * mm, "end": v(-106.36, 803.95) * mm});
            skLineSegment(sketch, "E26.0.21.0", {"start": v(-284.16, 143.55) * mm, "end": v(-55.56, 143.55) * mm});
            skLineSegment(sketch, "E26.0.21.1", {"start": v(-284.16, 194.35) * mm, "end": v(-55.56, 194.35) * mm});
            skLineSegment(sketch, "E26.0.21.2", {"start": v(-284.16, 245.15) * mm, "end": v(-55.56, 245.15) * mm});
            skLineSegment(sketch, "E26.0.21.3", {"start": v(-284.16, 295.95) * mm, "end": v(-55.56, 295.95) * mm});
            skLineSegment(sketch, "E26.0.21.4", {"start": v(-284.16, 346.75) * mm, "end": v(-55.56, 346.75) * mm});
            skLineSegment(sketch, "E26.0.21.5", {"start": v(-284.16, 397.55) * mm, "end": v(-55.56, 397.55) * mm});
            skLineSegment(sketch, "E26.0.21.6", {"start": v(-284.16, 448.35) * mm, "end": v(-55.56, 448.35) * mm});
            skLineSegment(sketch, "E26.0.21.7", {"start": v(-284.16, 499.15) * mm, "end": v(-55.56, 499.15) * mm});
            skLineSegment(sketch, "E26.0.21.8", {"start": v(-284.16, 549.95) * mm, "end": v(-55.56, 549.95) * mm});
            skLineSegment(sketch, "E26.0.21.9", {"start": v(-284.16, 600.75) * mm, "end": v(-55.56, 600.75) * mm});
            skLineSegment(sketch, "E26.0.21.10", {"start": v(-284.16, 651.55) * mm, "end": v(-55.56, 651.55) * mm});
            skLineSegment(sketch, "E26.0.21.11", {"start": v(-284.16, 702.35) * mm, "end": v(-55.56, 702.35) * mm});
            skLineSegment(sketch, "E26.0.21.12", {"start": v(-284.16, 753.15) * mm, "end": v(-55.56, 753.15) * mm});
            skLineSegment(sketch, "E26.0.21.13", {"start": v(-284.16, 803.95) * mm, "end": v(-55.56, 803.95) * mm});
            skLineSegment(sketch, "E27.direction1", {"start": v(-1350.96, 143.3) * mm, "end": v(-1325.56, 143.3) * mm, "construction": true});
            skSolve(sketch);
        }
        {
            var Q0;
            Q0=makeQuery(id+"F0.imprint","IMPRINT",FACE,{"disambiguationData":[TD([[makeQuery(id+"F0.imprint","IMPRINT",EDGE,{"derivedFrom":sQuery(id+"F0.wireOp",EDGE,"E0.bottom")}),-1.0]])]});
            extrude(context, id + "F1", {"entities" : qUnion([Q0]), "depth" : 18.26 * mm, "offsetDistance" : 25.4 * mm});
        }
    });
